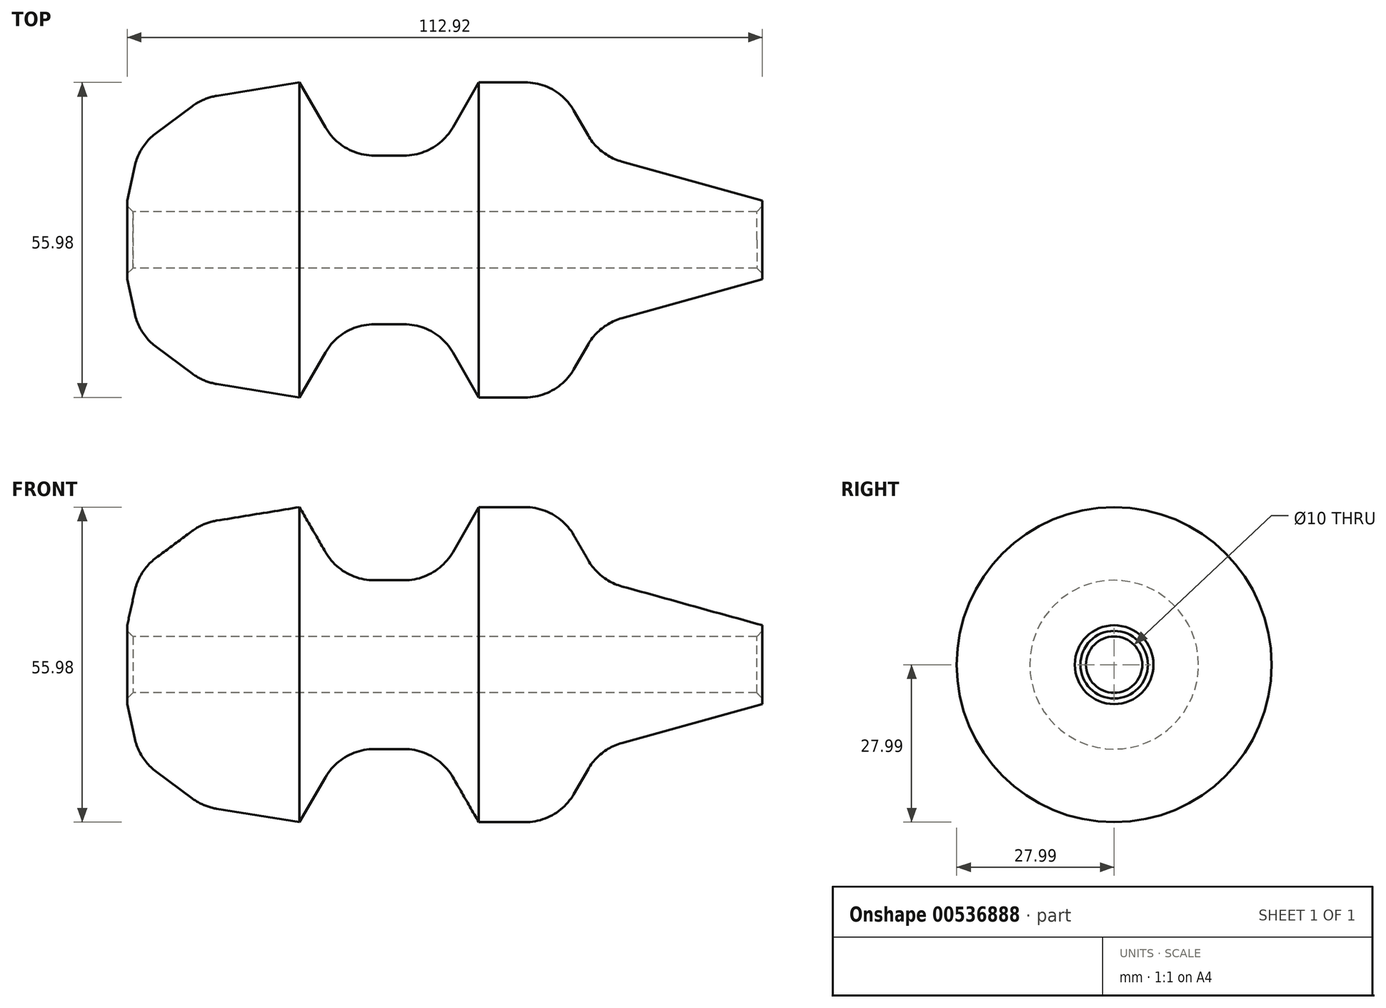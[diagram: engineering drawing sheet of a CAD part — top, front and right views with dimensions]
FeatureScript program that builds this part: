
annotation { "Feature Type Name" : "Feature", "Feature Type Description" : "" }
export const myFeature = defineFeature(function(context is Context, id is Id, definition is map)
    precondition{}
    {
        {
            var Q0;
            Q0=qCreatedBy(makeId("Front.planeOp"),FACE);
            var sketch = newSketch(context, id + "F0", { "sketchPlane" : qUnion([Q0])});
            skLineSegment(sketch, "E0", {"start": v(-73.53, 2) * mm, "end": v(-69.9, 18.6) * mm});
            skLineSegment(sketch, "E1", {"start": v(-69.9, 18.6) * mm, "end": v(-42.9, 23) * mm});
            skLineSegment(sketch, "E2", {"start": v(-42.9, 23) * mm, "end": v(-35.4, 10) * mm});
            skLineSegment(sketch, "E3", {"start": v(-35.4, 10) * mm, "end": v(-18.52, 10) * mm});
            skLineSegment(sketch, "E4", {"start": v(-18.52, 10) * mm, "end": v(-11.02, 23) * mm});
            skLineSegment(sketch, "E5", {"start": v(-11.02, 23) * mm, "end": v(2.98, 23) * mm});
            skLineSegment(sketch, "E6", {"start": v(2.98, 23) * mm, "end": v(10.48, 10) * mm});
            skLineSegment(sketch, "E7", {"start": v(10.48, 10) * mm, "end": v(39.4, 2) * mm});
            skLineSegment(sketch, "E8", {"start": v(39.4, 2) * mm, "end": v(39.4, 0) * mm});
            skLineSegment(sketch, "E9", {"start": v(39.4, 0) * mm, "end": v(-73.53, 0) * mm});
            skLineSegment(sketch, "E10", {"start": v(-73.53, 0) * mm, "end": v(-73.53, 2) * mm});
            skLineSegment(sketch, "E11", {"start": v(-84.22, -5) * mm, "end": v(57.05, -5) * mm, "construction": true});
            skSolve(sketch);
        }
        {
            var Q0;
            Q0=makeQuery(id+"F0.imprint","IMPRINT",FACE,{"disambiguationData":[TD([[makeQuery(id+"F0.imprint","IMPRINT",EDGE,{"derivedFrom":sQuery(id+"F0.wireOp",EDGE,"E0")}),-1.0]])]});
            var Q1;
            Q1=sQuery(id+"F0.wireOp",EDGE,"E11");
            revolve(context, id + "F1", {"entities" : qUnion([Q0]), "axis" : qUnion([Q1]), "revolveType" : RevolveType.FULL});
        }
        {
            var Q0;
            Q0=makeQuery(id+"F1.opRevolve","SWEPT_EDGE",EDGE,{"disambiguationData":[OSD([sQuery(id+"F0.wireOp",EDGE,"E0"),sQuery(id+"F0.wireOp",EDGE,"E1")])]});
            chamfer(context, id + "F2", {"entities" : qUnion([Q0]), "chamferType" : ChamferType.TWO_OFFSETS, "width1" : 7 * mm, "oppositeDirection" : false, "width2" : 10 * mm, "tangentPropagation" : true});
        }
        {
            var Q0;
            Q0=makeQuery(id+"F1.opRevolve","SWEPT_EDGE",EDGE,{"disambiguationData":[OSD([sQuery(id+"F0.wireOp",EDGE,"E2"),sQuery(id+"F0.wireOp",EDGE,"E3")])]});
            var Q1;
            Q1=makeQuery(id+"F1.opRevolve","SWEPT_EDGE",EDGE,{"disambiguationData":[OSD([sQuery(id+"F0.wireOp",EDGE,"E3"),sQuery(id+"F0.wireOp",EDGE,"E4")])]});
            var Q2;
            Q2=makeQuery(id+"F1.opRevolve","SWEPT_EDGE",EDGE,{"disambiguationData":[OSD([sQuery(id+"F0.wireOp",EDGE,"E6"),sQuery(id+"F0.wireOp",EDGE,"E7")])]});
            var Q3;
            {var subQ0=sQuery(id+"F0.wireOp",EDGE,"E1");Q3=makeQuery(id+"F2.opChamfer","BLEND_EDGE",EDGE,{"blendedFrom":[makeQuery(id+"F1.opRevolve","SWEPT_EDGE",EDGE,{"disambiguationData":[OSD([sQuery(id+"F0.wireOp",EDGE,"E0"),subQ0])]}),makeQuery(id+"F1.opRevolve","SWEPT_FACE",FACE,{"disambiguationData":[OSD([subQ0])]})],"blendedInto":[makeQuery(id+"F1.opRevolve","SWEPT_FACE",FACE,{"disambiguationData":[OSD([subQ0])]})]});}
            var Q4;
            Q4=makeQuery(id+"F1.opRevolve","SWEPT_EDGE",EDGE,{"disambiguationData":[OSD([sQuery(id+"F0.wireOp",EDGE,"E5"),sQuery(id+"F0.wireOp",EDGE,"E6")])]});
            var Q5;
            {var subQ0=sQuery(id+"F0.wireOp",EDGE,"E0");Q5=makeQuery(id+"F2.opChamfer","BLEND_EDGE",EDGE,{"blendedFrom":[makeQuery(id+"F1.opRevolve","SWEPT_EDGE",EDGE,{"disambiguationData":[OSD([subQ0,sQuery(id+"F0.wireOp",EDGE,"E1")])]}),makeQuery(id+"F1.opRevolve","SWEPT_FACE",FACE,{"disambiguationData":[OSD([subQ0])]})],"blendedInto":[makeQuery(id+"F1.opRevolve","SWEPT_FACE",FACE,{"disambiguationData":[OSD([subQ0])]})]});}
            fillet(context, id + "F3", {"entities" : qUnion([Q0, Q1, Q2, Q3, Q4, Q5]), "radius" : 10 * mm, "tangentPropagation" : true, "allowEdgeOverflow" : false});
        }
        {
            var Q0;
            Q0=makeQuery(id+"F1.opRevolve","SWEPT_EDGE",EDGE,{"disambiguationData":[OSD([sQuery(id+"F0.wireOp",EDGE,"E9"),sQuery(id+"F0.wireOp",EDGE,"E10")])]});
            var Q1;
            Q1=makeQuery(id+"F1.opRevolve","SWEPT_EDGE",EDGE,{"disambiguationData":[OSD([sQuery(id+"F0.wireOp",EDGE,"E8"),sQuery(id+"F0.wireOp",EDGE,"E9")])]});
            chamfer(context, id + "F4", {"entities" : qUnion([Q0, Q1]), "width" : 1 * mm, "tangentPropagation" : true});
        }
    });
